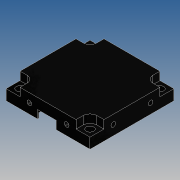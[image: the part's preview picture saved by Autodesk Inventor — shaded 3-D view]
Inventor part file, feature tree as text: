
AUTODESK INVENTOR PART (.ipt)
format: ipt  version: 2015 SP1 (Build 190203100, 203)  size: 290,304 bytes
history: native  units: mm
features: sketch x6, extrude x4, hole x2, plane x1, mirror x1, pattern_circular x1
ambient origin geometry x8: Origin, YZ Plane, XZ Plane, XY Plane, X Axis, Y Axis, Z Axis, Center Point
bodies: Solid1 (feature_tree)
feature tree (15):
  extrude  "Extrusion1"  Depth=18.0mm
  hole  "Hole1"  [1 undecoded]
  extrude  "Extrusion2"  Depth=3.0mm
  extrude  "Extrusion3"  Depth=3.5mm TaperAngle=360.0deg
  hole  "M3/6/10"  [1 undecoded]
  plane  "Work Plane1"
  mirror  "Mirror1"
  pattern_circular  "Circular Pattern1"  [2 undecoded]
  extrude  "Extrusion4"  Depth=2.0mm TaperAngle=0.0deg
  sketch  "Sketch1"  dims[d0=18.0mm d1=18.0mm]
  sketch  "Sketch2"  dims[d2=8.0mm d3=0.0mm d4=15.0mm]
  sketch  "Sketch3"  dims[d5=15.0mm]
  sketch  "Sketch4"  dims[d6=3.2mm d7=6.0mm d8=6.0mm d9=2.0mm d10=90.0deg d11=8.0mm d12=20.594885mm d13=3.0mm]
  sketch  "Sketch5"  dims[d14=3.5mm d15=0.0mm d16=40.0mm d17=360.0deg]
  sketch  "Sketch7"  dims[d19=0.5mm d20=0.5mm d21=3.0mm d22=2.0mm d23=0.0mm d24=8.0mm d25=3.8mm d26=2.0mm d27=6.0mm d28=6.0mm d29=2.0mm d30=90.0deg d31=2.0mm d32=0.0mm d33=9.0mm d34=8.0mm d35=2.0mm d36=18.5mm d37=3.5mm d38=0.0mm d39=1.0mm d40=1.0mm]
note: 4 required parameter values undecoded (feature->parameter linkage not recoverable at this tier; creation-order binding heuristic only, values carry confidence <= 0.55)
